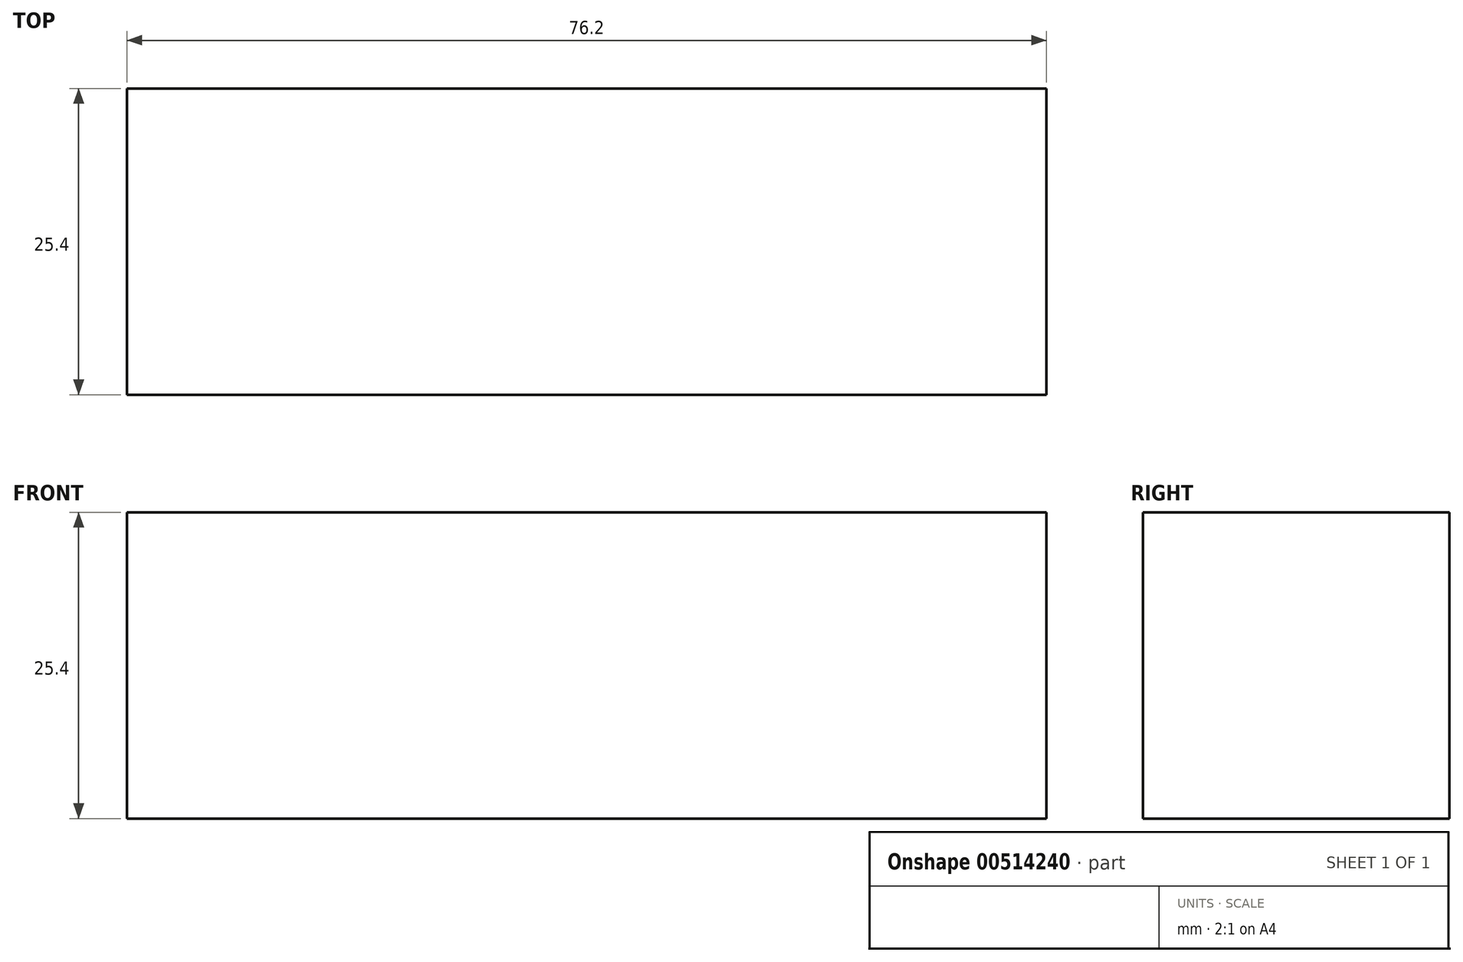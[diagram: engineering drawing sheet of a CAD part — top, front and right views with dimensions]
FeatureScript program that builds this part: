
annotation { "Feature Type Name" : "Feature", "Feature Type Description" : "" }
export const myFeature = defineFeature(function(context is Context, id is Id, definition is map)
    precondition{}
    {
        {
            var Q0;
            Q0=qCreatedBy(makeId("Front.planeOp"),FACE);
            var sketch = newSketch(context, id + "F0", { "sketchPlane" : qUnion([Q0])});
            skLineSegment(sketch, "E0.bottom", {"start": v(-44.17, 0) * mm, "end": v(32.03, 0) * mm});
            skLineSegment(sketch, "E0.top", {"start": v(-44.17, 25.4) * mm, "end": v(32.03, 25.4) * mm});
            skLineSegment(sketch, "E0.left", {"start": v(-44.17, 0) * mm, "end": v(-44.17, 25.4) * mm});
            skLineSegment(sketch, "E0.right", {"start": v(32.03, 0) * mm, "end": v(32.03, 25.4) * mm});
            skLineSegment(sketch, "E1.bottom", {"start": v(-18.77, 25.4) * mm, "end": v(6.63, 25.4) * mm});
            skLineSegment(sketch, "E1.top", {"start": v(-18.77, 50.8) * mm, "end": v(6.63, 50.8) * mm});
            skLineSegment(sketch, "E1.left", {"start": v(-18.77, 25.4) * mm, "end": v(-18.77, 50.8) * mm});
            skLineSegment(sketch, "E1.right", {"start": v(6.63, 25.4) * mm, "end": v(6.63, 50.8) * mm});
            skSolve(sketch);
        }
        {
            var Q0;
            Q0=makeQuery(id+"F0.imprint","IMPRINT",FACE,{"disambiguationData":[TD([[makeQuery(id+"F0.imprint","IMPRINT",EDGE,{"derivedFrom":sQuery(id+"F0.wireOp",EDGE,"E0.bottom")}),1.0]])]});
            var Q1;
            Q1=makeQuery(id+"F0.imprint","IMPRINT",FACE,{"disambiguationData":[TD([[makeQuery(id+"F0.imprint","IMPRINT",EDGE,{"derivedFrom":sQuery(id+"F0.wireOp",EDGE,"E1.bottom")}),1.0]])]});
            extrude(context, id + "F1", {"entities" : qUnion([Q0, Q1]), "depth" : 25.4 * mm});
        }
    });
